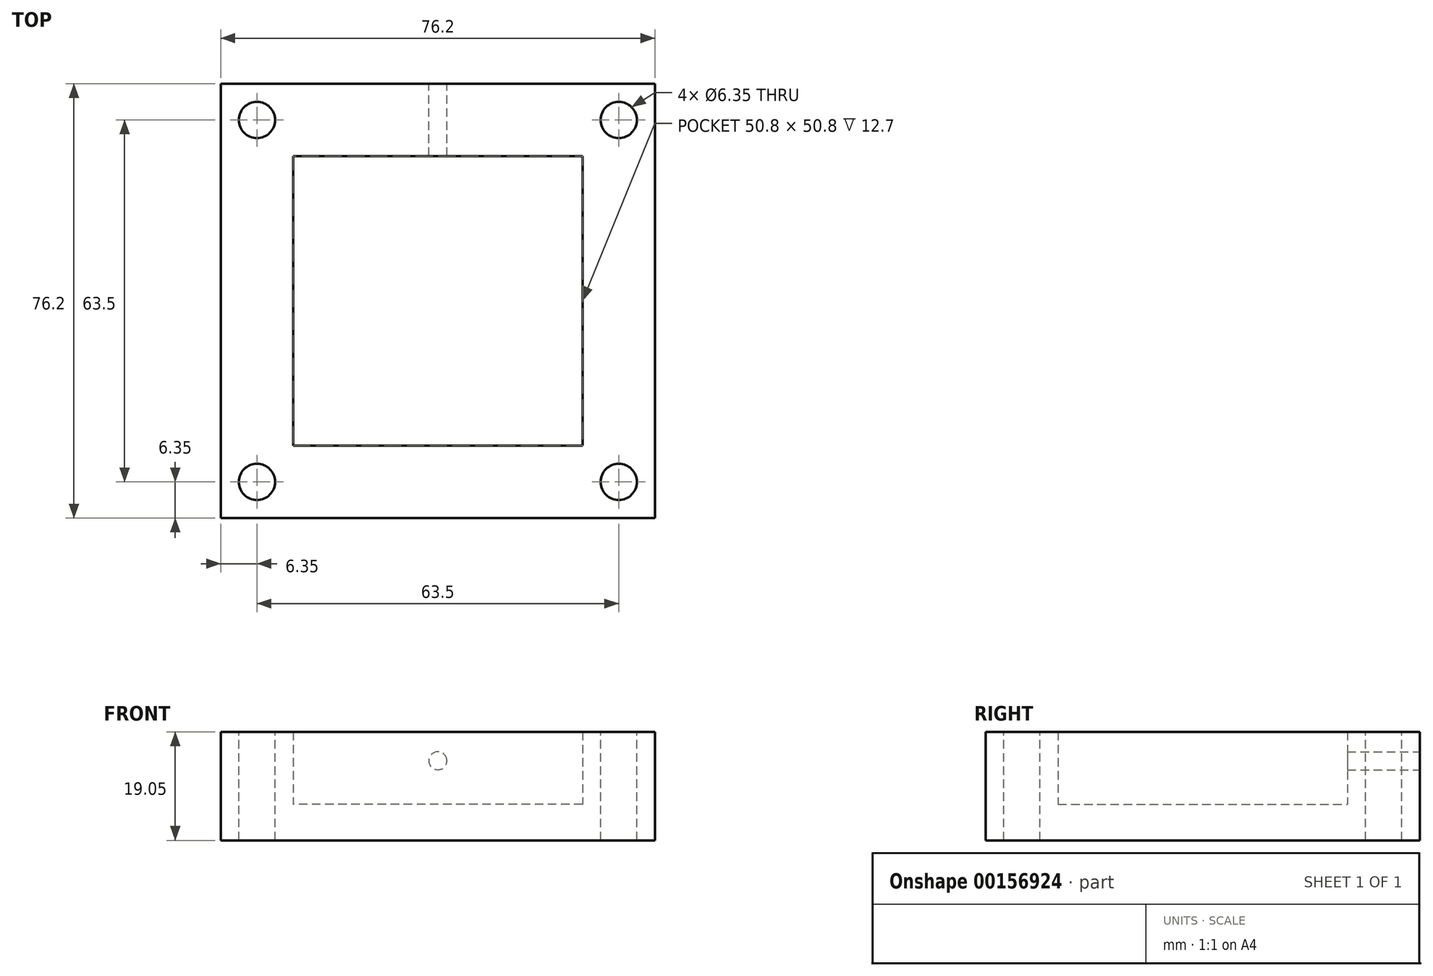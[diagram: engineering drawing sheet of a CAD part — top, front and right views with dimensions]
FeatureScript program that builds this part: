
annotation { "Feature Type Name" : "Feature", "Feature Type Description" : "" }
export const myFeature = defineFeature(function(context is Context, id is Id, definition is map)
    precondition{}
    {
        {
            var Q0;
            Q0=qCreatedBy(makeId("Top.planeOp"),FACE);
            var sketch = newSketch(context, id + "F0", { "sketchPlane" : qUnion([Q0])});
            skLineSegment(sketch, "E0.bottom", {"start": v(-38.1, 38.1) * mm, "end": v(38.1, 38.1) * mm});
            skLineSegment(sketch, "E0.top", {"start": v(-38.1, -38.1) * mm, "end": v(38.1, -38.1) * mm});
            skLineSegment(sketch, "E0.left", {"start": v(-38.1, 38.1) * mm, "end": v(-38.1, -38.1) * mm});
            skLineSegment(sketch, "E0.right", {"start": v(38.1, 38.1) * mm, "end": v(38.1, -38.1) * mm});
            skLineSegment(sketch, "E1.bottom", {"start": v(-25.4, 25.4) * mm, "end": v(25.4, 25.4) * mm});
            skLineSegment(sketch, "E1.top", {"start": v(-25.4, -25.4) * mm, "end": v(25.4, -25.4) * mm});
            skLineSegment(sketch, "E1.left", {"start": v(-25.4, 25.4) * mm, "end": v(-25.4, -25.4) * mm});
            skLineSegment(sketch, "E1.right", {"start": v(25.4, 25.4) * mm, "end": v(25.4, -25.4) * mm});
            skLineSegment(sketch, "E2", {"start": v(0, 38.1) * mm, "end": v(0, 25.4) * mm, "construction": true});
            skLineSegment(sketch, "E3", {"start": v(0, 25.4) * mm, "end": v(0, 38.1) * mm, "construction": true});
            skLineSegment(sketch, "E4", {"start": v(-38.1, 0) * mm, "end": v(-25.4, 0) * mm, "construction": true});
            skSolve(sketch);
        }
        {
            var Q0;
            Q0=makeQuery(id+"F0.imprint","IMPRINT",FACE,{"disambiguationData":[TD([[makeQuery(id+"F0.imprint","IMPRINT",EDGE,{"derivedFrom":sQuery(id+"F0.wireOp",EDGE,"E0.bottom")}),-1.0]])]});
            var Q1;
            Q1=makeQuery(id+"F0.imprint","IMPRINT",FACE,{"disambiguationData":[TD([[makeQuery(id+"F0.imprint","IMPRINT",EDGE,{"derivedFrom":sQuery(id+"F0.wireOp",EDGE,"E1.bottom")}),-1.0]])]});
            extrude(context, id + "F1", {"entities" : qUnion([Q0, Q1]), "depth" : 6.35 * mm});
        }
        {
            var Q0;
            Q0=makeQuery(id+"F0.imprint","IMPRINT",FACE,{"disambiguationData":[TD([[makeQuery(id+"F0.imprint","IMPRINT",EDGE,{"derivedFrom":sQuery(id+"F0.wireOp",EDGE,"E0.bottom")}),-1.0]])]});
            extrude(context, id + "F2", {"entities" : qUnion([Q0]), "operationType" : NewBodyOperationType.ADD, "depth" : 19.05 * mm});
        }
        {
            var Q0;
            {var subQ0=sQuery(id+"F0.wireOp",EDGE,"E0.bottom");Q0=makeQuery(id+"F2.boolean.opBoolean","MERGE",FACE,{"derivedFrom":[makeQuery(id+"F1.opExtrude","SWEPT_FACE",FACE,{"disambiguationData":[OSD([subQ0])]}),makeQuery(id+"F2.opExtrude","SWEPT_FACE",FACE,{"disambiguationData":[OSD([subQ0])]})]});}
            var sketch = newSketch(context, id + "F3", { "sketchPlane" : qUnion([Q0])});
            skCircle(sketch, "E5", {"center": v(0, 13.97) * mm, "radius": 1.59 * mm});
            skSolve(sketch);
        }
        {
            var Q0;
            Q0=makeQuery(id+"F3.imprint","IMPRINT",FACE,{"disambiguationData":[TD([[makeQuery(id+"F3.imprint","IMPRINT",EDGE,{"derivedFrom":sQuery(id+"F3.wireOp",EDGE,"E5")}),1.0]])]});
            extrude(context, id + "F4", {"entities" : qUnion([Q0]), "operationType" : NewBodyOperationType.REMOVE, "oppositeDirection" : true, "depth" : 25.4 * mm});
        }
        {
            var Q0;
            Q0=makeQuery(id+"F2.opExtrude","CAP_FACE",FACE,{"disambiguationData":[OSD([sQuery(id+"F0.wireOp",EDGE,"E0.bottom"),sQuery(id+"F0.wireOp",EDGE,"E0.top"),sQuery(id+"F0.wireOp",EDGE,"E0.left"),sQuery(id+"F0.wireOp",EDGE,"E0.right"),sQuery(id+"F0.wireOp",EDGE,"E1.bottom"),sQuery(id+"F0.wireOp",EDGE,"E1.top"),sQuery(id+"F0.wireOp",EDGE,"E1.left"),sQuery(id+"F0.wireOp",EDGE,"E1.right")])],"isStart":false});
            var sketch = newSketch(context, id + "F5", { "sketchPlane" : qUnion([Q0])});
            skLineSegment(sketch, "E6.bottom", {"start": v(-38.1, 38.1) * mm, "end": v(-25.4, 38.1) * mm});
            skLineSegment(sketch, "E6.top", {"start": v(-38.1, 25.4) * mm, "end": v(-25.4, 25.4) * mm});
            skLineSegment(sketch, "E6.left", {"start": v(-38.1, 38.1) * mm, "end": v(-38.1, 25.4) * mm});
            skLineSegment(sketch, "E6.right", {"start": v(-25.4, 38.1) * mm, "end": v(-25.4, 25.4) * mm});
            skLineSegment(sketch, "E7.bottom", {"start": v(25.4, 25.4) * mm, "end": v(38.1, 25.4) * mm});
            skLineSegment(sketch, "E7.top", {"start": v(25.4, 38.1) * mm, "end": v(38.1, 38.1) * mm});
            skLineSegment(sketch, "E7.left", {"start": v(25.4, 25.4) * mm, "end": v(25.4, 38.1) * mm});
            skLineSegment(sketch, "E7.right", {"start": v(38.1, 25.4) * mm, "end": v(38.1, 38.1) * mm});
            skLineSegment(sketch, "E8.bottom", {"start": v(25.4, -25.4) * mm, "end": v(38.1, -25.4) * mm});
            skLineSegment(sketch, "E8.top", {"start": v(25.4, -38.1) * mm, "end": v(38.1, -38.1) * mm});
            skLineSegment(sketch, "E8.left", {"start": v(25.4, -25.4) * mm, "end": v(25.4, -38.1) * mm});
            skLineSegment(sketch, "E8.right", {"start": v(38.1, -25.4) * mm, "end": v(38.1, -38.1) * mm});
            skLineSegment(sketch, "E9.bottom", {"start": v(-25.4, -25.4) * mm, "end": v(-38.1, -25.4) * mm});
            skLineSegment(sketch, "E9.top", {"start": v(-25.4, -38.1) * mm, "end": v(-38.1, -38.1) * mm});
            skLineSegment(sketch, "E9.left", {"start": v(-25.4, -25.4) * mm, "end": v(-25.4, -38.1) * mm});
            skLineSegment(sketch, "E9.right", {"start": v(-38.1, -25.4) * mm, "end": v(-38.1, -38.1) * mm});
            skCircle(sketch, "E10", {"center": v(-31.75, 31.75) * mm, "radius": 3.18 * mm});
            skCircle(sketch, "E11", {"center": v(31.75, 31.75) * mm, "radius": 3.18 * mm});
            skCircle(sketch, "E12", {"center": v(31.75, -31.75) * mm, "radius": 317.5 * mm});
            skCircle(sketch, "E13", {"center": v(-31.75, -31.75) * mm, "radius": 3.18 * mm});
            skCircle(sketch, "E14", {"center": v(31.75, -31.75) * mm, "radius": 3.18 * mm});
            skSolve(sketch);
        }
        {
            var Q0;
            Q0=makeQuery(id+"F5.imprint","IMPRINT",FACE,{"disambiguationData":[TD([[makeQuery(id+"F5.imprint","IMPRINT",EDGE,{"derivedFrom":sQuery(id+"F5.wireOp",EDGE,"E10")}),1.0]])]});
            var Q1;
            Q1=makeQuery(id+"F5.imprint","IMPRINT",FACE,{"disambiguationData":[TD([[makeQuery(id+"F5.imprint","IMPRINT",EDGE,{"derivedFrom":sQuery(id+"F5.wireOp",EDGE,"E11")}),1.0]])]});
            var Q2;
            Q2=makeQuery(id+"F5.imprint","IMPRINT",FACE,{"disambiguationData":[TD([[makeQuery(id+"F5.imprint","IMPRINT",EDGE,{"derivedFrom":sQuery(id+"F5.wireOp",EDGE,"E14")}),1.0]])]});
            var Q3;
            Q3=makeQuery(id+"F5.imprint","IMPRINT",FACE,{"disambiguationData":[TD([[makeQuery(id+"F5.imprint","IMPRINT",EDGE,{"derivedFrom":sQuery(id+"F5.wireOp",EDGE,"E13")}),1.0]])]});
            extrude(context, id + "F6", {"entities" : qUnion([Q0, Q1, Q2, Q3]), "operationType" : NewBodyOperationType.REMOVE, "endBound" : BoundingType.THROUGH_ALL, "oppositeDirection" : true, "depth" : 25.4 * mm});
        }
    });
